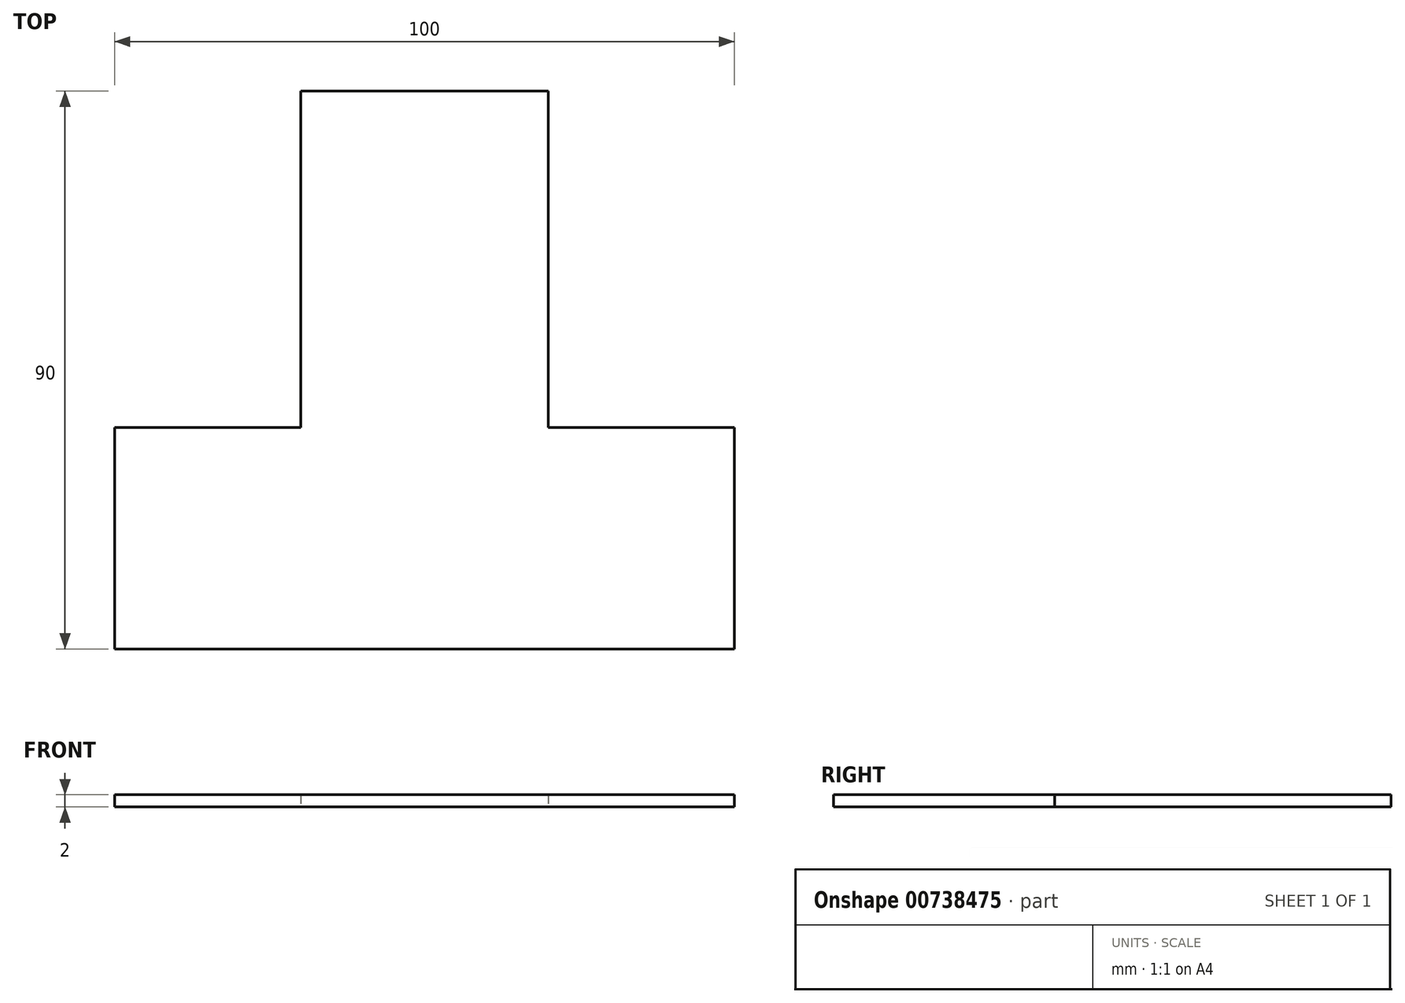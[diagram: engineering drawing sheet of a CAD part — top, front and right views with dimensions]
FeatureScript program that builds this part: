
annotation { "Feature Type Name" : "Feature", "Feature Type Description" : "" }
export const myFeature = defineFeature(function(context is Context, id is Id, definition is map)
    precondition{}
    {
        {
            var Q0;
            Q0=qCreatedBy(makeId("Top.planeOp"),FACE);
            var sketch = newSketch(context, id + "F0", { "sketchPlane" : qUnion([Q0])});
            skLineSegment(sketch, "E0.bottom", {"start": v(-20, 70) * mm, "end": v(20, 70) * mm});
            skLineSegment(sketch, "E0.top", {"start": v(-20, -20) * mm, "end": v(20, -20) * mm});
            skLineSegment(sketch, "E0.left", {"start": v(-20, 70) * mm, "end": v(-20, -20) * mm});
            skLineSegment(sketch, "E0.right", {"start": v(20, 70) * mm, "end": v(20, -20) * mm});
            skLineSegment(sketch, "E1", {"start": v(-20, -20) * mm, "end": v(-50, -20) * mm});
            skLineSegment(sketch, "E2", {"start": v(-50, -20) * mm, "end": v(-50, 15.72) * mm});
            skLineSegment(sketch, "E3", {"start": v(-50, 15.72) * mm, "end": v(50, 15.72) * mm});
            skLineSegment(sketch, "E4", {"start": v(50, 15.72) * mm, "end": v(50, -20) * mm});
            skLineSegment(sketch, "E5", {"start": v(50, -20) * mm, "end": v(20, -20) * mm});
            skSolve(sketch);
        }
        {
            var Q0;
            {var subQ0=sQuery(id+"F0.wireOp",EDGE,"E0.bottom");Q0=makeQuery(id+"F0.imprint","IMPRINT",FACE,{"disambiguationData":[TD([[makeQuery(id+"F0.imprint","IMPRINT",EDGE,{"derivedFrom":subQ0}),-1.0]])]});}
            var Q1;
            {var subQ0=sQuery(id+"F0.wireOp",EDGE,"E1");Q1=makeQuery(id+"F0.imprint","IMPRINT",FACE,{"disambiguationData":[TD([[makeQuery(id+"F0.imprint","IMPRINT",EDGE,{"derivedFrom":subQ0}),-1.0]])]});}
            var Q2;
            {var subQ0=sQuery(id+"F0.wireOp",EDGE,"E0.top");Q2=makeQuery(id+"F0.imprint","IMPRINT",FACE,{"disambiguationData":[TD([[makeQuery(id+"F0.imprint","IMPRINT",EDGE,{"derivedFrom":subQ0}),1.0]])]});}
            var Q3;
            {var subQ4=sQuery(id+"F0.wireOp",EDGE,"E4");Q3=makeQuery(id+"F0.imprint","IMPRINT",FACE,{"disambiguationData":[TD([[makeQuery(id+"F0.imprint","IMPRINT",EDGE,{"derivedFrom":subQ4}),-1.0]])]});}
            extrude(context, id + "F1", {"entities" : qUnion([Q0, Q1, Q2, Q3]), "depth" : 2 * mm, "offsetDistance" : 25 * mm});
        }
    });
